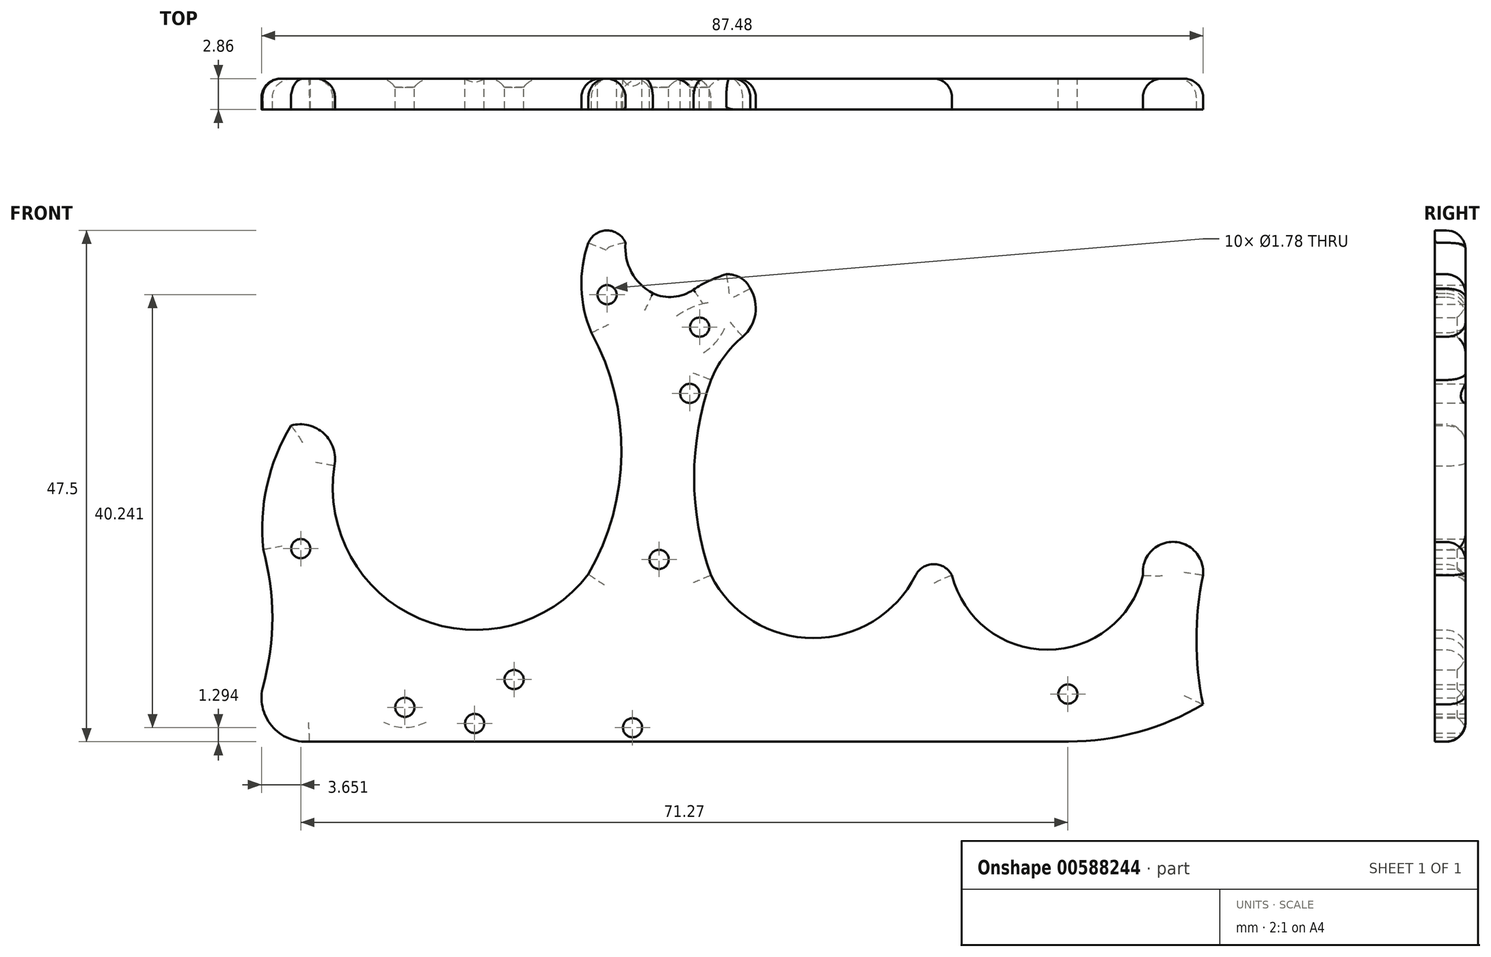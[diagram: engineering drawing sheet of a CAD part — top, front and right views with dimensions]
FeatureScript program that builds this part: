
annotation { "Feature Type Name" : "Feature", "Feature Type Description" : "" }
export const myFeature = defineFeature(function(context is Context, id is Id, definition is map)
    precondition{}
    {
        {
            var Q0;
            Q0=qCreatedBy(makeId("Front.planeOp"),FACE);
            var sketch = newSketch(context, id + "F0", { "sketchPlane" : qUnion([Q0])});
            skArc(sketch, "E0", {"start": v(-15.69, 7.63) * mm, "mid": v(-12.62, 18.81) * mm, "end": v(-15.4, 30.08) * mm});
            skArc(sketch, "E1", {"start": v(-39.29, 17.7) * mm, "mid": v(-31.4, 3.51) * mm, "end": v(-15.69, 7.63) * mm});
            skArc(sketch, "E2", {"start": v(41.4, 7.53) * mm, "mid": v(38.62, 10.63) * mm, "end": v(35.84, 7.53) * mm});
            skArc(sketch, "E3", {"start": v(-4.3, 25.68) * mm, "mid": v(-5.87, 16.6) * mm, "end": v(-4.3, 7.53) * mm});
            skArc(sketch, "E4", {"start": v(-15.69, 38.42) * mm, "mid": v(-16.34, 34.22) * mm, "end": v(-15.4, 30.08) * mm});
            skLineSegment(sketch, "E5", {"start": v(-7.91, -7.91) * mm, "end": v(28.92, -7.91) * mm});
            skArc(sketch, "E6", {"start": v(-43.31, 21.44) * mm, "mid": v(-45.54, 15.9) * mm, "end": v(-45.9, 9.93) * mm});
            skArc(sketch, "E7", {"start": v(-45.9, -2.73) * mm, "mid": v(-45.03, 3.6) * mm, "end": v(-45.9, 9.93) * mm});
            skLineSegment(sketch, "E8", {"start": v(-7.91, -7.91) * mm, "end": v(-41.59, -7.91) * mm});
            skArc(sketch, "E9", {"start": v(-45.9, -2.73) * mm, "mid": v(-45.1, -6.46) * mm, "end": v(-41.59, -7.91) * mm});
            skArc(sketch, "E10", {"start": v(41.4, 7.53) * mm, "mid": v(40.8, 1.52) * mm, "end": v(41.4, -4.48) * mm});
            skArc(sketch, "E11", {"start": v(28.92, -7.91) * mm, "mid": v(35.4, -7.04) * mm, "end": v(41.4, -4.48) * mm});
            skArc(sketch, "E12", {"start": v(-4.3, 7.53) * mm, "mid": v(5.2, 1.69) * mm, "end": v(14.7, 7.53) * mm});
            skArc(sketch, "E13", {"start": v(18.09, 7.53) * mm, "mid": v(26.96, 0.6) * mm, "end": v(35.84, 7.53) * mm});
            skArc(sketch, "E14", {"start": v(14.7, 7.53) * mm, "mid": v(16.4, 8.57) * mm, "end": v(18.09, 7.53) * mm});
            skPoint(sketch, "E15", {"position": v(-22.6, -2.16) * mm});
            skArc(sketch, "E16", {"start": v(-39.29, 17.7) * mm, "mid": v(-40.25, 20.7) * mm, "end": v(-43.31, 21.44) * mm});
            skArc(sketch, "E17", {"start": v(-1.35, 29.7) * mm, "mid": v(-3.07, 27.87) * mm, "end": v(-4.3, 25.68) * mm});
            skArc(sketch, "E18", {"start": v(-1.35, 29.7) * mm, "mid": v(-0.18, 31.8) * mm, "end": v(-0.64, 34.17) * mm});
            skArc(sketch, "E19", {"start": v(-0.64, 34.17) * mm, "mid": v(-1.55, 35.18) * mm, "end": v(-2.88, 35.5) * mm});
            skArc(sketch, "E20", {"start": v(-2.88, 35.5) * mm, "mid": v(-4.46, 34.9) * mm, "end": v(-5.93, 34.07) * mm});
            skArc(sketch, "E21", {"start": v(-9.7, 33.73) * mm, "mid": v(-7.77, 33.4) * mm, "end": v(-5.93, 34.07) * mm});
            skArc(sketch, "E22", {"start": v(-12.23, 38.42) * mm, "mid": v(-11.68, 35.69) * mm, "end": v(-9.7, 33.73) * mm});
            skArc(sketch, "E23", {"start": v(-12.23, 38.42) * mm, "mid": v(-13.96, 39.57) * mm, "end": v(-15.69, 38.42) * mm});
            skPoint(sketch, "E24", {"position": v(-5.35, 30.58) * mm});
            skPoint(sketch, "E25", {"position": v(-9.12, 9) * mm});
            skPoint(sketch, "E26", {"position": v(-32.74, -4.74) * mm});
            skPoint(sketch, "E27", {"position": v(28.86, -3.5) * mm});
            skPoint(sketch, "E28", {"position": v(-42.4, 10) * mm});
            skPoint(sketch, "E29", {"position": v(-13.95, 33.6) * mm});
            skPoint(sketch, "E30", {"position": v(-26.26, -6.24) * mm});
            skPoint(sketch, "E31", {"position": v(-11.59, -6.64) * mm});
            skPoint(sketch, "E32", {"position": v(-6.27, 24.43) * mm});
            skSolve(sketch);
        }
        {
            var Q0;
            Q0=makeQuery(id+"F0.imprint","IMPRINT",FACE,{"disambiguationData":[TD([[makeQuery(id+"F0.imprint","IMPRINT",EDGE,{"derivedFrom":sQuery(id+"F0.wireOp",EDGE,"E0")}),-1.0]])]});
            extrude(context, id + "F1", {"entities" : qUnion([Q0]), "depth" : 2.86 * mm, "offsetDistance" : 25.4 * mm});
        }
        {
            var Q0;
            Q0=sQuery(id+"F0.wireOp",VERTEX,"4d9ed20c-a050-41b1-a726-ba9a68d03454");
            var Q1;
            Q1=sQuery(id+"F0.wireOp",VERTEX,"f05e3413-97fa-4317-9460-9a704415e28e");
            var Q2;
            Q2=sQuery(id+"F0.wireOp",VERTEX,"E15");
            var Q3;
            Q3=sQuery(id+"F0.wireOp",VERTEX,"ca89f7f3-d3c6-4f0c-a5c2-640b6aec9d28");
            var Q4;
            Q4=sQuery(id+"F0.wireOp",VERTEX,"cdc7b90f-4f78-4515-b2b2-9dd8b976f43d");
            var Q5;
            Q5=sQuery(id+"F0.wireOp",VERTEX,"E24");
            var Q6;
            Q6=sQuery(id+"F0.wireOp",VERTEX,"0d2d3b97-50c2-489a-9959-e3951f0aeffd");
            var Q7;
            Q7=sQuery(id+"F0.wireOp",VERTEX,"E25");
            var Q8;
            Q8=sQuery(id+"F0.wireOp",VERTEX,"9ed7a9c9-4632-4ed3-ae27-16036feed5c8");
            var Q9;
            Q9=sQuery(id+"F0.wireOp",VERTEX,"9a4e39e4-95d2-4212-8172-b782fcab2ba0");
            var Q10;
            Q10=sQuery(id+"F0.wireOp",VERTEX,"E26");
            var Q11;
            Q11=makeQuery(id+"F1.opExtrude","SWEPT_BODY",BODY,{"disambiguationData":[OSD([sQuery(id+"F0.wireOp",EDGE,"E0"),sQuery(id+"F0.wireOp",EDGE,"E1"),sQuery(id+"F0.wireOp",EDGE,"E2"),sQuery(id+"F0.wireOp",EDGE,"E3"),sQuery(id+"F0.wireOp",EDGE,"3EEqmpVa-sYtS-nlyx-7368-GrBW48sy61ME"),sQuery(id+"F0.wireOp",EDGE,"UqaOKMos-FZ6l-7GI9-J2aR-ZYlEZ6ikFnGb"),sQuery(id+"F0.wireOp",EDGE,"SGjXxW1m-KlGl-boIV-9Onv-vCJ5jf5MEAHU"),sQuery(id+"F0.wireOp",EDGE,"487ae1e9-430a-4b7e-8a56-f4b97fb80ecd"),sQuery(id+"F0.wireOp",EDGE,"E4"),sQuery(id+"F0.wireOp",EDGE,"E5"),sQuery(id+"F0.wireOp",EDGE,"E6"),sQuery(id+"F0.wireOp",EDGE,"E7"),sQuery(id+"F0.wireOp",EDGE,"E8"),sQuery(id+"F0.wireOp",EDGE,"E9"),sQuery(id+"F0.wireOp",EDGE,"E10"),sQuery(id+"F0.wireOp",EDGE,"E11"),sQuery(id+"F0.wireOp",EDGE,"E12"),sQuery(id+"F0.wireOp",EDGE,"E13"),sQuery(id+"F0.wireOp",EDGE,"E14"),sQuery(id+"F0.wireOp",EDGE,"E16")])]});
            hole(context, id + "F2", {"style" : HoleStyle.C_SINK, "endStyle" : HoleEndStyle.THROUGH, "oppositeDirection" : true, "holeDiameter" : 1.78 * mm, "cSinkDiameter" : 3.17 * mm, "cSinkAngle" : 82 * degree, "majorDiameter" : 2.18 * mm, "isTappedThrough" : true, "tappedDepth" : 12.7 * mm, "tapClearance" : 3, "locations" : qUnion([Q0, Q1, Q2, Q3, Q4, Q5, Q6, Q7, Q8, Q9, Q10]), "scope" : qUnion([Q11])});
        }
        {
            var Q0;
            Q0=makeQuery(id+"F1.opExtrude","CAP_FACE",FACE,{"disambiguationData":[OSD([sQuery(id+"F0.wireOp",EDGE,"E0"),sQuery(id+"F0.wireOp",EDGE,"E1"),sQuery(id+"F0.wireOp",EDGE,"E2"),sQuery(id+"F0.wireOp",EDGE,"E3"),sQuery(id+"F0.wireOp",EDGE,"E4"),sQuery(id+"F0.wireOp",EDGE,"E5"),sQuery(id+"F0.wireOp",EDGE,"E6"),sQuery(id+"F0.wireOp",EDGE,"E7"),sQuery(id+"F0.wireOp",EDGE,"E8"),sQuery(id+"F0.wireOp",EDGE,"E9"),sQuery(id+"F0.wireOp",EDGE,"E10"),sQuery(id+"F0.wireOp",EDGE,"E11"),sQuery(id+"F0.wireOp",EDGE,"E12"),sQuery(id+"F0.wireOp",EDGE,"E13"),sQuery(id+"F0.wireOp",EDGE,"E14"),sQuery(id+"F0.wireOp",EDGE,"E16"),sQuery(id+"F0.wireOp",EDGE,"E17"),sQuery(id+"F0.wireOp",EDGE,"E18"),sQuery(id+"F0.wireOp",EDGE,"E19"),sQuery(id+"F0.wireOp",EDGE,"E20"),sQuery(id+"F0.wireOp",EDGE,"E21"),sQuery(id+"F0.wireOp",EDGE,"E22"),sQuery(id+"F0.wireOp",EDGE,"E23")])],"isStart":true});
            fillet(context, id + "F3", {"entities" : qUnion([Q0]), "radius" : 1.78 * mm, "tangentPropagation" : true, "allowEdgeOverflow" : false});
        }
        {
            var Q0;
            Q0=makeQuery(id+"F1.opExtrude","CAP_EDGE",EDGE,{"disambiguationData":[OSD([sQuery(id+"F0.wireOp",EDGE,"E22")])],"isStart":false});
            var Q1;
            Q1=makeQuery(id+"F1.opExtrude","CAP_EDGE",EDGE,{"disambiguationData":[OSD([sQuery(id+"F0.wireOp",EDGE,"E21")])],"isStart":false});
            var Q2;
            Q2=makeQuery(id+"F1.opExtrude","CAP_EDGE",EDGE,{"disambiguationData":[OSD([sQuery(id+"F0.wireOp",EDGE,"E20")])],"isStart":false});
            fillet(context, id + "F4", {"entities" : qUnion([Q0, Q1, Q2]), "radius" : 0.25 * mm, "tangentPropagation" : true, "allowEdgeOverflow" : false});
        }
        {
            var Q0;
            Q0=sQuery(id+"F0.wireOp",VERTEX,"E27");
            var Q1;
            Q1=sQuery(id+"F0.wireOp",VERTEX,"b014f50a-9f28-43bc-b15e-8ee6fc23f1b4");
            var Q2;
            Q2=sQuery(id+"F0.wireOp",VERTEX,"b526cf91-38f9-4e19-8765-be2269e85942");
            var Q3;
            Q3=sQuery(id+"F0.wireOp",VERTEX,"99efb21d-b27a-46c7-803b-7dd9ae423e38");
            var Q4;
            Q4=sQuery(id+"F0.wireOp",VERTEX,"E28");
            var Q5;
            Q5=sQuery(id+"F0.wireOp",VERTEX,"E29");
            var Q6;
            Q6=sQuery(id+"F0.wireOp",VERTEX,"E30");
            var Q7;
            Q7=sQuery(id+"F0.wireOp",VERTEX,"E31");
            var Q8;
            Q8=sQuery(id+"F0.wireOp",VERTEX,"E32");
            var Q9;
            Q9=makeQuery(id+"F1.opExtrude","SWEPT_BODY",BODY,{"disambiguationData":[OSD([sQuery(id+"F0.wireOp",EDGE,"E0"),sQuery(id+"F0.wireOp",EDGE,"E1"),sQuery(id+"F0.wireOp",EDGE,"E2"),sQuery(id+"F0.wireOp",EDGE,"E3"),sQuery(id+"F0.wireOp",EDGE,"E4"),sQuery(id+"F0.wireOp",EDGE,"E5"),sQuery(id+"F0.wireOp",EDGE,"E6"),sQuery(id+"F0.wireOp",EDGE,"E7"),sQuery(id+"F0.wireOp",EDGE,"E8"),sQuery(id+"F0.wireOp",EDGE,"E9"),sQuery(id+"F0.wireOp",EDGE,"E10"),sQuery(id+"F0.wireOp",EDGE,"E11"),sQuery(id+"F0.wireOp",EDGE,"E12"),sQuery(id+"F0.wireOp",EDGE,"E13"),sQuery(id+"F0.wireOp",EDGE,"E14"),sQuery(id+"F0.wireOp",EDGE,"E16"),sQuery(id+"F0.wireOp",EDGE,"E17"),sQuery(id+"F0.wireOp",EDGE,"E18"),sQuery(id+"F0.wireOp",EDGE,"E19"),sQuery(id+"F0.wireOp",EDGE,"E20"),sQuery(id+"F0.wireOp",EDGE,"E21"),sQuery(id+"F0.wireOp",EDGE,"E22"),sQuery(id+"F0.wireOp",EDGE,"E23")])]});
            hole(context, id + "F5", {"style" : HoleStyle.SIMPLE, "endStyle" : HoleEndStyle.THROUGH, "oppositeDirection" : true, "holeDiameter" : 1.78 * mm, "majorDiameter" : 6.35 * mm, "isTappedThrough" : true, "tappedDepth" : 12.7 * mm, "tapClearance" : 3, "locations" : qUnion([Q0, Q1, Q2, Q3, Q4, Q5, Q6, Q7, Q8]), "scope" : qUnion([Q9])});
        }
    });
